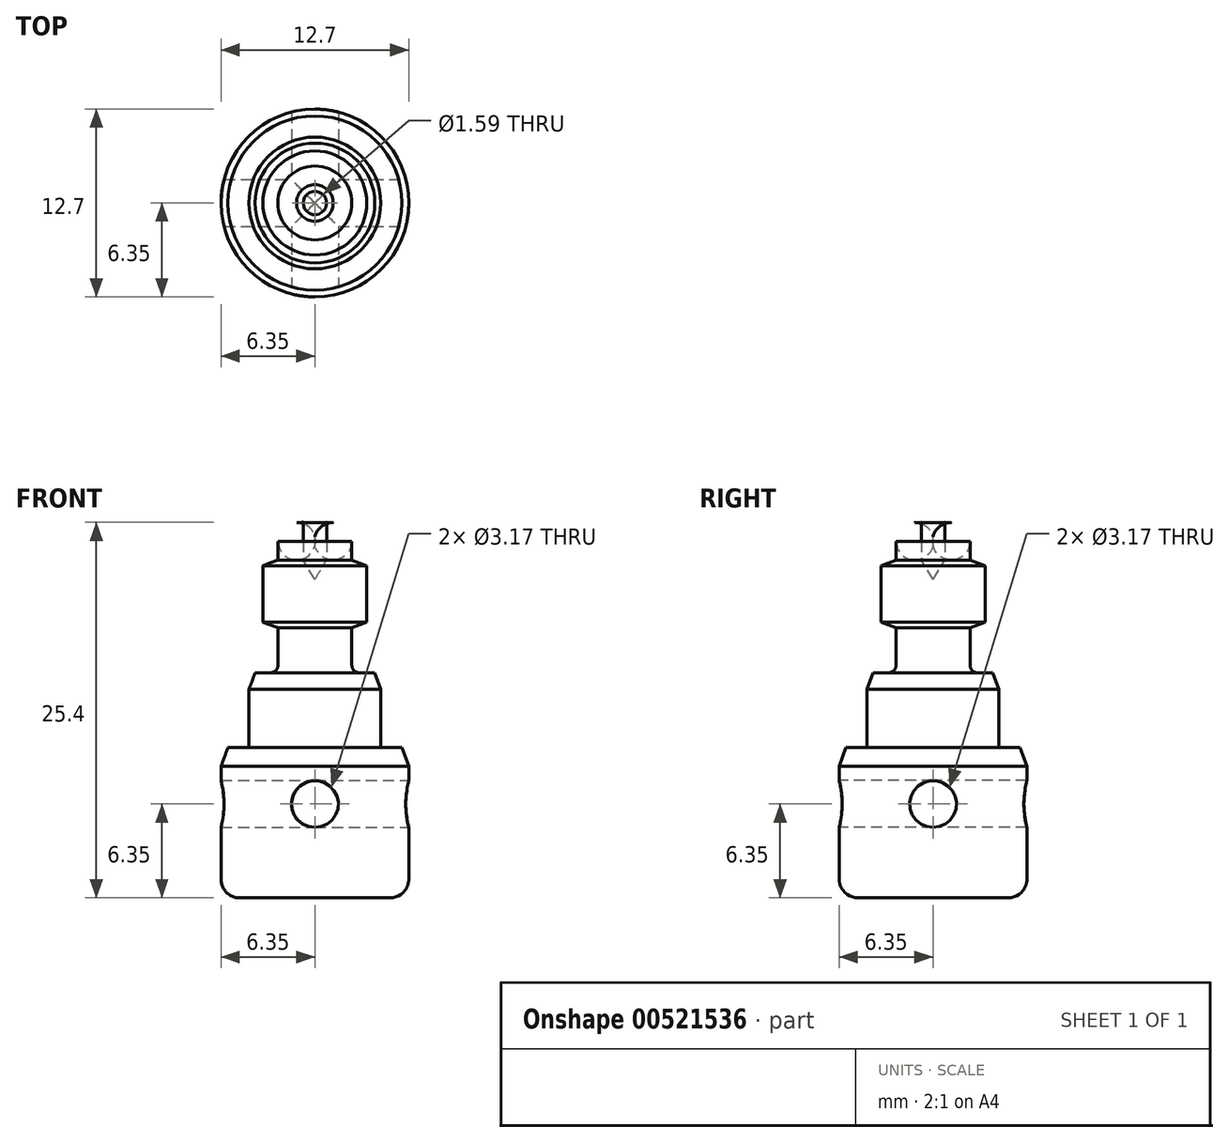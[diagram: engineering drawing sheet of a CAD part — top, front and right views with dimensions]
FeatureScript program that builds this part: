
annotation { "Feature Type Name" : "Feature", "Feature Type Description" : "" }
export const myFeature = defineFeature(function(context is Context, id is Id, definition is map)
    precondition{}
    {
        {
            var Q0;
            Q0=qCreatedBy(makeId("Front.planeOp"),FACE);
            var sketch = newSketch(context, id + "F0", { "sketchPlane" : qUnion([Q0])});
            skLineSegment(sketch, "E0", {"start": v(0, 0) * mm, "end": v(0, 25.4) * mm});
            skLineSegment(sketch, "E1", {"start": v(0, 0) * mm, "end": v(-5.08, 0) * mm});
            skLineSegment(sketch, "E2", {"start": v(-6.35, 1.27) * mm, "end": v(-6.35, 8.9) * mm});
            skLineSegment(sketch, "E3", {"start": v(-5.89, 10.16) * mm, "end": v(-4.45, 10.16) * mm});
            skLineSegment(sketch, "E4", {"start": v(-4.45, 10.16) * mm, "end": v(-4.45, 14.11) * mm});
            skLineSegment(sketch, "E5", {"start": v(-4.05, 15.23) * mm, "end": v(-3, 15.23) * mm});
            skLineSegment(sketch, "E6", {"start": v(-2.5, 15.74) * mm, "end": v(-2.5, 18.28) * mm});
            skLineSegment(sketch, "E7", {"start": v(-3.52, 18.65) * mm, "end": v(-3.52, 22.47) * mm});
            skLineSegment(sketch, "E8", {"start": v(-2.5, 22.85) * mm, "end": v(-2.5, 24.12) * mm});
            skLineSegment(sketch, "E9", {"start": v(-1.24, 25.4) * mm, "end": v(0, 25.4) * mm});
            skPoint(sketch, "E10.visualSharp", {"position": v(-6.35, 0) * mm});
            skArc(sketch, "E10.filletArc", {"start": v(-6.35, 1.27) * mm, "mid": v(-5.98, 0.37) * mm, "end": v(-5.08, 0) * mm});
            skPoint(sketch, "E11.visualSharp", {"position": v(-2.5, 15.23) * mm});
            skArc(sketch, "E11.filletArc", {"start": v(-3, 15.23) * mm, "mid": v(-2.65, 15.38) * mm, "end": v(-2.5, 15.74) * mm});
            skLineSegment(sketch, "E12", {"start": v(-4.45, 15.47) * mm, "end": v(-4.05, 15.47) * mm, "construction": true});
            skPoint(sketch, "E13", {"position": v(-4.05, 15.23) * mm});
            skLineSegment(sketch, "E14", {"start": v(-4.05, 15.23) * mm, "end": v(-4.05, 13.77) * mm, "construction": true});
            skLineSegment(sketch, "E15", {"start": v(-6.35, 10.16) * mm, "end": v(-6.93, 10.16) * mm, "construction": true});
            skLineSegment(sketch, "E16", {"start": v(-6.93, 10.16) * mm, "end": v(-6.93, 8.9) * mm, "construction": true});
            skPoint(sketch, "E17", {"position": v(-6.35, 8.9) * mm});
            skLineSegment(sketch, "E18", {"start": v(-6.35, 8.9) * mm, "end": v(-5.89, 10.16) * mm});
            skLineSegment(sketch, "E19", {"start": v(-4.45, 14.11) * mm, "end": v(-4.05, 15.23) * mm});
            skPoint(sketch, "E20.orphan", {"position": v(-4.45, 15.23) * mm});
            skPoint(sketch, "E21.visualSharp", {"position": v(-2.5, 25.39) * mm});
            skArc(sketch, "E21.filletArc", {"start": v(-1.24, 25.4) * mm, "mid": v(-2.13, 25.02) * mm, "end": v(-2.5, 24.12) * mm});
            skLineSegment(sketch, "E22", {"start": v(-3.52, 18.65) * mm, "end": v(-2.5, 18.28) * mm});
            skLineSegment(sketch, "E23", {"start": v(-3.52, 22.47) * mm, "end": v(-2.5, 22.85) * mm});
            skPoint(sketch, "E24.end.orphan", {"position": v(-3.77, 18.65) * mm});
            skPoint(sketch, "E25.end.orphan", {"position": v(-3.77, 22.47) * mm});
            skPoint(sketch, "E26.end.orphan", {"position": v(-3.77, 22.85) * mm});
            skSolve(sketch);
        }
        {
            var Q0;
            Q0=makeQuery(id+"F0.imprint","IMPRINT",FACE,{"disambiguationData":[TD([[makeQuery(id+"F0.imprint","IMPRINT",EDGE,{"derivedFrom":sQuery(id+"F0.wireOp",EDGE,"E0")}),1.0]])]});
            var Q1;
            Q1=sQuery(id+"F0.wireOp",EDGE,"E0");
            revolve(context, id + "F1", {"entities" : qUnion([Q0]), "axis" : qUnion([Q1]), "revolveType" : RevolveType.FULL});
        }
        {
            var Q0;
            Q0=qCreatedBy(makeId("Front.planeOp"),FACE);
            var sketch = newSketch(context, id + "F2", { "sketchPlane" : qUnion([Q0])});
            skLineSegment(sketch, "E27.bottom", {"start": v(0, 25.4) * mm, "end": v(0.8, 25.4) * mm});
            skLineSegment(sketch, "E27.left", {"start": v(0, 25.4) * mm, "end": v(0, 22.86) * mm});
            skLineSegment(sketch, "E27.right", {"start": v(0.8, 25.4) * mm, "end": v(0.8, 22.85) * mm});
            skLineSegment(sketch, "E28", {"start": v(0.8, 22.85) * mm, "end": v(0, 21.54) * mm});
            skLineSegment(sketch, "E29", {"start": v(0, 22.86) * mm, "end": v(0, 21.54) * mm});
            skSolve(sketch);
        }
        {
            var Q0;
            Q0 = qSketchRegion(id + "F2", true);
            var Q1;
            Q1=sQuery(id+"F2.wireOp",EDGE,"E27.left");
            revolve(context, id + "F3", {"operationType" : NewBodyOperationType.REMOVE, "entities" : qUnion([Q0]), "axis" : qUnion([Q1]), "revolveType" : RevolveType.FULL, "oppositeDirection" : true});
        }
        {
            var Q0;
            Q0=qCreatedBy(makeId("Front.planeOp"),FACE);
            cPlane(context, id + "F4", {"entities" : qUnion([Q0]), "cplaneType" : CPlaneType.OFFSET, "offset" : 6.35 * mm, "width" : 152.4 * mm, "height" : 152.4 * mm});
        }
        {
            var Q0;
            Q0=qCreatedBy(id+"F4.planeOp",FACE);
            var sketch = newSketch(context, id + "F5", { "sketchPlane" : qUnion([Q0])});
            skLineSegment(sketch, "E30", {"start": v(0, 0) * mm, "end": v(0, 6.35) * mm, "construction": true});
            skCircle(sketch, "E31", {"center": v(0, 6.35) * mm, "radius": 1.59 * mm});
            skSolve(sketch);
        }
        {
            var Q0;
            Q0 = qSketchRegion(id + "F5", true);
            extrude(context, id + "F6", {"entities" : qUnion([Q0]), "operationType" : NewBodyOperationType.REMOVE, "endBound" : BoundingType.THROUGH_ALL, "oppositeDirection" : true, "depth" : 25.4 * mm, "offsetDistance" : 25.4 * mm});
        }
        {
            var Q0;
            Q0=qCreatedBy(makeId("Right.planeOp"),FACE);
            cPlane(context, id + "F7", {"entities" : qUnion([Q0]), "cplaneType" : CPlaneType.OFFSET, "offset" : 25.4 * mm, "width" : 152.4 * mm, "height" : 152.4 * mm});
        }
        {
            var Q0;
            Q0=qCreatedBy(id+"F7.planeOp",FACE);
            var sketch = newSketch(context, id + "F8", { "sketchPlane" : qUnion([Q0])});
            skLineSegment(sketch, "E32", {"start": v(0, 0) * mm, "end": v(0, 6.35) * mm, "construction": true});
            skCircle(sketch, "E33", {"center": v(0, 6.35) * mm, "radius": 1.59 * mm});
            skSolve(sketch);
        }
        {
            var Q0;
            Q0 = qSketchRegion(id + "F8", true);
            extrude(context, id + "F9", {"entities" : qUnion([Q0]), "operationType" : NewBodyOperationType.REMOVE, "endBound" : BoundingType.THROUGH_ALL, "oppositeDirection" : true, "depth" : 25.4 * mm, "offsetDistance" : 25.4 * mm});
        }
    });
